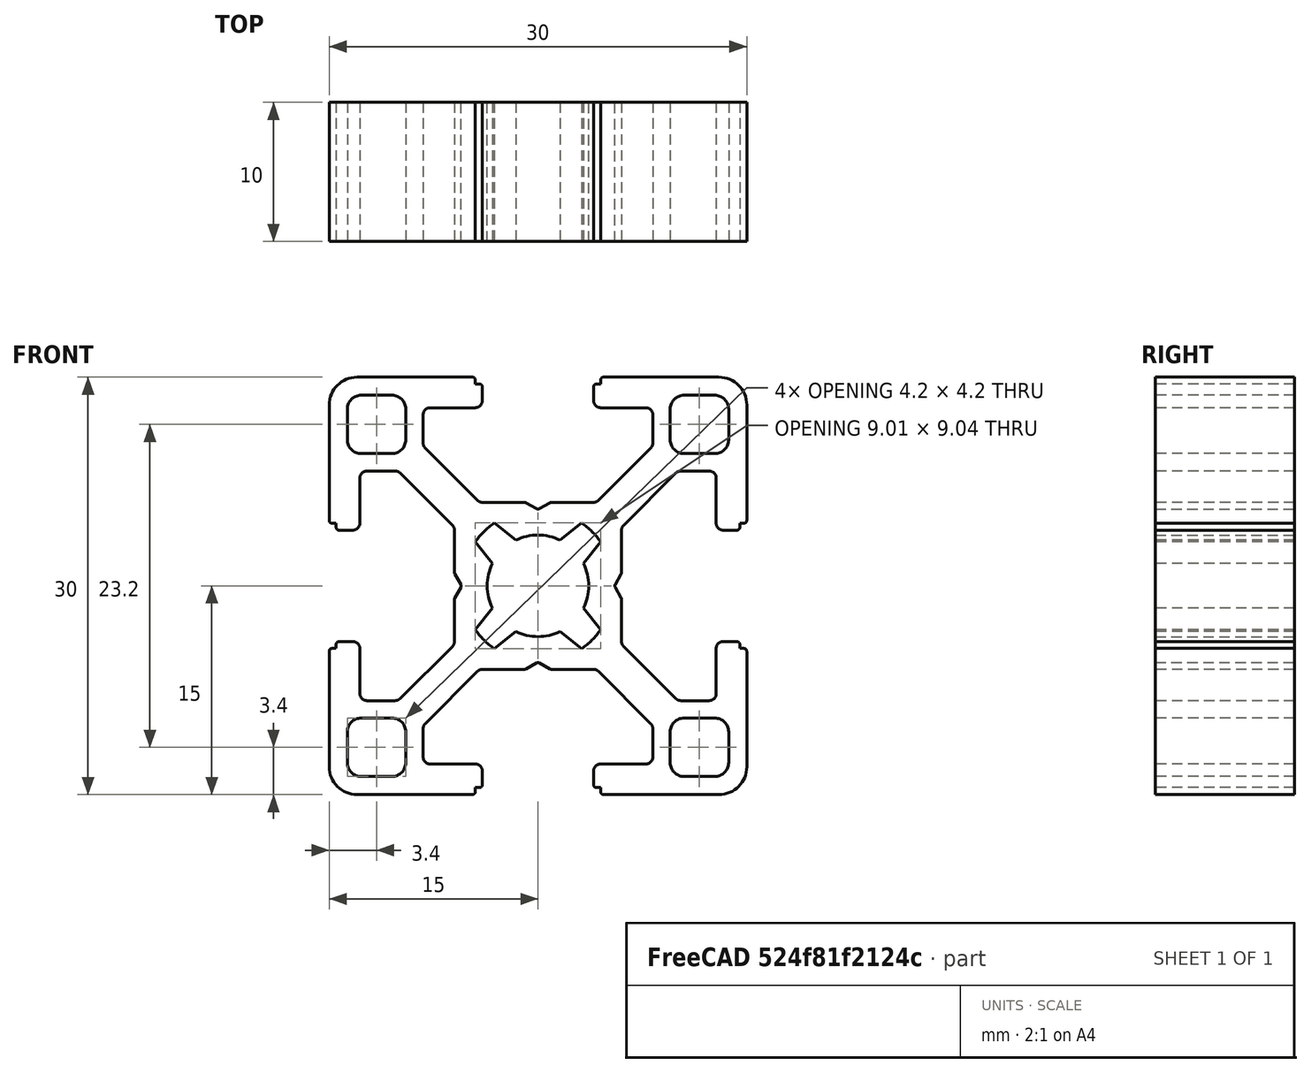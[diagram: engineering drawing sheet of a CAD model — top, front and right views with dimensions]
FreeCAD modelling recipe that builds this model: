
FCSTD DOCUMENT  (FreeCAD 0.19R21329 (Git))
Label: AP3030S8
Comment: FreeCAD-Library by episource -- https://github.com/episource/FreeCAD-Library
License: Creative Commons Attribution
LicenseURL: http://creativecommons.org/licenses/by/4.0/
objects: PartDesign::CoordinateSystem×15, TechDraw::DrawViewDimension×6, Sketcher::SketchObject×1, TechDraw::DrawSVGTemplate×1, PartDesign::Pad×1, PartDesign::Body×1, TechDraw::DrawViewPart×1, TechDraw::DrawViewClip×1, TechDraw::DrawPage×1, PartDesign::Line×1, App::DocumentObjectGroup×1, App::Part×1
note: 20 computed .brp shape members not serialized (recipe doc carries the construction recipe); baked Part::Feature solids carry a one-line shape summary decoded from their .brp

FEATURE [Sketcher::SketchObject] Sketch007  label="AP3030N8"
  MapMode = 3
  Placement = pos=(0,0,0) rot=(1,0,0;1.5708rad)
  sketch-geometry (184):
    g0: LineSegment StartX=15 StartY=13 StartZ=0 EndX=15 EndY=4.7 EndZ=0
    g1: ArcOfCircle CenterX=13 CenterY=13 CenterZ=0 NormalX=0 NormalY=0 NormalZ=1 AngleXU=2.16005e-11 Radius=2 StartAngle=0 EndAngle=1.5708
    g2: LineSegment StartX=4.7 StartY=15 StartZ=0 EndX=13 EndY=15 EndZ=0
    g3: ArcOfCircle CenterX=4.7 CenterY=14.8 CenterZ=0 NormalX=0 NormalY=0 NormalZ=1 AngleXU=1.5708 Radius=0.2 StartAngle=0 EndAngle=1.5708
    g4: LineSegment StartX=4.5 StartY=14.5 StartZ=0 EndX=4.5 EndY=14.8 EndZ=0
    g5: LineSegment StartX=4.2 StartY=14.5 StartZ=0 EndX=4.5 EndY=14.5 EndZ=0
    g6: ArcOfCircle CenterX=4.2 CenterY=14.3 CenterZ=0 NormalX=0 NormalY=0 NormalZ=1 AngleXU=1.5708 Radius=0.2 StartAngle=0 EndAngle=1.5708
    g7: LineSegment StartX=4 StartY=13.3 StartZ=0 EndX=4 EndY=14.3 EndZ=0
    g8: ArcOfCircle CenterX=4.5 CenterY=13.3 CenterZ=0 NormalX=0 NormalY=0 NormalZ=1 AngleXU=3.14159 Radius=0.5 StartAngle=0 EndAngle=1.5708
    g9: LineSegment StartX=7.75 StartY=12.8 StartZ=0 EndX=4.5 EndY=12.8 EndZ=0
    g10: ArcOfCircle CenterX=7.75 CenterY=12.3 CenterZ=0 NormalX=0 NormalY=0 NormalZ=1 AngleXU=-3.14159 Radius=0.5 StartAngle=3.14159 EndAngle=4.71239
    g11: LineSegment StartX=8.25 StartY=10.2569 StartZ=0 EndX=8.25 EndY=12.3 EndZ=0
    g12: ArcOfCircle CenterX=7.75 CenterY=10.2569 CenterZ=0 NormalX=0 NormalY=0 NormalZ=1 AngleXU=2.35675 Radius=0.5 StartAngle=3.14159 EndAngle=3.92644
    g13: LineSegment StartX=4.35095 StartY=6.14664 StartZ=0 EndX=8.10375 EndY=9.90359 EndZ=0
    g14: ArcOfCircle CenterX=3.9972 CenterY=6.5 CenterZ=0 NormalX=0 NormalY=0 NormalZ=1 AngleXU=1.5708 Radius=0.5 StartAngle=3.14159 EndAngle=3.92754
    g15: LineSegment StartX=0.953191 StartY=6 StartZ=0 EndX=3.9972 EndY=6 EndZ=0
    g16: ArcOfCircle CenterX=0.953191 CenterY=5.8 CenterZ=0 NormalX=0 NormalY=0 NormalZ=1 AngleXU=1.5708 Radius=0.2 StartAngle=0 EndAngle=0.519868
    g17: LineSegment StartX=0.0993536 StartY=5.54172 StartZ=0 EndX=0.853837 EndY=5.97358 EndZ=0
    g18: ArcOfCircle CenterX=4.3595e-07 CenterY=5.7153 CenterZ=0 NormalX=0 NormalY=0 NormalZ=1 AngleXU=1.05093 Radius=0.2 StartAngle=3.14159 EndAngle=4.18133
    g19: LineSegment StartX=-0.853837 StartY=5.97358 StartZ=0 EndX=-0.0993527 EndY=5.54172 EndZ=0
    g20: ArcOfCircle CenterX=-0.95319 CenterY=5.8 CenterZ=0 NormalX=0 NormalY=0 NormalZ=1 AngleXU=1.05093 Radius=0.2 StartAngle=0 EndAngle=0.519868
    g21: LineSegment StartX=-3.9972 StartY=6 StartZ=0 EndX=-0.95319 EndY=6 EndZ=0
    g22: ArcOfCircle CenterX=-3.9972 CenterY=6.5 CenterZ=0 NormalX=0 NormalY=0 NormalZ=1 AngleXU=0.784847 Radius=0.5 StartAngle=3.14159 EndAngle=3.92754
    g23: LineSegment StartX=-8.10375 StartY=9.90359 StartZ=0 EndX=-4.35095 EndY=6.14664 EndZ=0
    g24: ArcOfCircle CenterX=-7.75 CenterY=10.2569 CenterZ=0 NormalX=0 NormalY=0 NormalZ=1 AngleXU=1.25056e-11 Radius=0.5 StartAngle=3.14159 EndAngle=3.92644
    g25: LineSegment StartX=-8.25 StartY=12.3 StartZ=0 EndX=-8.25 EndY=10.2569 EndZ=0
    g26: ArcOfCircle CenterX=-7.75 CenterY=12.3 CenterZ=0 NormalX=0 NormalY=0 NormalZ=1 AngleXU=-1.5708 Radius=0.5 StartAngle=3.14159 EndAngle=4.71239
    g27: LineSegment StartX=-4.5 StartY=12.8 StartZ=0 EndX=-7.75 EndY=12.8 EndZ=0
    g28: ArcOfCircle CenterX=-4.5 CenterY=13.3 CenterZ=0 NormalX=0 NormalY=0 NormalZ=1 AngleXU=-1.5708 Radius=0.5 StartAngle=0 EndAngle=1.5708
    g29: LineSegment StartX=-4 StartY=14.3 StartZ=0 EndX=-4 EndY=13.3 EndZ=0
    g30: ArcOfCircle CenterX=-4.2 CenterY=14.3 CenterZ=0 NormalX=0 NormalY=0 NormalZ=1 AngleXU=0 Radius=0.2 StartAngle=0 EndAngle=1.5708
    g31: LineSegment StartX=-4.5 StartY=14.5 StartZ=0 EndX=-4.2 EndY=14.5 EndZ=0
    g32: LineSegment StartX=-4.5 StartY=14.8 StartZ=0 EndX=-4.5 EndY=14.5 EndZ=0
    g33: ArcOfCircle CenterX=-4.7 CenterY=14.8 CenterZ=0 NormalX=0 NormalY=0 NormalZ=1 AngleXU=-3.9222e-10 Radius=0.2 StartAngle=0 EndAngle=1.5708
    g34: LineSegment StartX=-13 StartY=15 StartZ=0 EndX=-4.7 EndY=15 EndZ=0
    g35: ArcOfCircle CenterX=-13 CenterY=13 CenterZ=0 NormalX=0 NormalY=0 NormalZ=1 AngleXU=1.5708 Radius=2 StartAngle=0 EndAngle=1.5708
    g36: LineSegment StartX=-15 StartY=4.7 StartZ=0 EndX=-15 EndY=13 EndZ=0
    g37: ArcOfCircle CenterX=-14.8 CenterY=4.7 CenterZ=0 NormalX=0 NormalY=0 NormalZ=1 AngleXU=-3.14159 Radius=0.2 StartAngle=0 EndAngle=1.5708
    g38: LineSegment StartX=-14.5 StartY=4.5 StartZ=0 EndX=-14.8 EndY=4.5 EndZ=0
    g39: LineSegment StartX=-14.5 StartY=4.2 StartZ=0 EndX=-14.5 EndY=4.5 EndZ=0
    g40: ArcOfCircle CenterX=-14.3 CenterY=4.2 CenterZ=0 NormalX=0 NormalY=0 NormalZ=1 AngleXU=-3.14159 Radius=0.2 StartAngle=0 EndAngle=1.5708
    g41: LineSegment StartX=-13.3 StartY=4 StartZ=0 EndX=-14.3 EndY=4 EndZ=0
    g42: ArcOfCircle CenterX=-13.3 CenterY=4.5 CenterZ=0 NormalX=0 NormalY=0 NormalZ=1 AngleXU=-1.5708 Radius=0.5 StartAngle=0 EndAngle=1.5708
    g43: LineSegment StartX=-12.8 StartY=7.75 StartZ=0 EndX=-12.8 EndY=4.5 EndZ=0
    g44: ArcOfCircle CenterX=-12.3 CenterY=7.75 CenterZ=0 NormalX=0 NormalY=0 NormalZ=1 AngleXU=-1.5708 Radius=0.5 StartAngle=3.14159 EndAngle=4.71239
    g45: LineSegment StartX=-10.2569 StartY=8.25 StartZ=0 EndX=-12.3 EndY=8.25 EndZ=0
    g46: ArcOfCircle CenterX=-10.2569 CenterY=7.75 CenterZ=0 NormalX=0 NormalY=0 NormalZ=1 AngleXU=-2.35564 Radius=0.5 StartAngle=3.14159 EndAngle=3.92644
    g47: LineSegment StartX=-6.14664 StartY=4.35095 StartZ=0 EndX=-9.90359 EndY=8.10375 EndZ=0
    g48: ArcOfCircle CenterX=-6.5 CenterY=3.9972 CenterZ=0 NormalX=0 NormalY=0 NormalZ=1 AngleXU=-3.14159 Radius=0.5 StartAngle=3.14159 EndAngle=3.92754
    g49: LineSegment StartX=-6 StartY=0.95319 StartZ=0 EndX=-6 EndY=3.9972 EndZ=0
    g50: ArcOfCircle CenterX=-5.8 CenterY=0.95319 CenterZ=0 NormalX=0 NormalY=0 NormalZ=1 AngleXU=-3.14159 Radius=0.2 StartAngle=0 EndAngle=0.519868
    g51: LineSegment StartX=-5.54172 StartY=0.0993532 StartZ=0 EndX=-5.97358 EndY=0.853837 EndZ=0
    g52: ArcOfCircle CenterX=-5.7153 CenterY=-1.603e-10 CenterZ=0 NormalX=0 NormalY=0 NormalZ=1 AngleXU=2.62172 Radius=0.2 StartAngle=3.14159 EndAngle=4.18133
    g53: LineSegment StartX=-5.97358 StartY=-0.853837 StartZ=0 EndX=-5.54172 EndY=-0.0993532 EndZ=0
    g54: ArcOfCircle CenterX=-5.8 CenterY=-0.95319 CenterZ=0 NormalX=0 NormalY=0 NormalZ=1 AngleXU=2.62172 Radius=0.2 StartAngle=0 EndAngle=0.519868
    g55: LineSegment StartX=-6 StartY=-3.9972 StartZ=0 EndX=-6 EndY=-0.95319 EndZ=0
    g56: ArcOfCircle CenterX=-6.5 CenterY=-3.9972 CenterZ=0 NormalX=0 NormalY=0 NormalZ=1 AngleXU=2.35564 Radius=0.5 StartAngle=3.14159 EndAngle=3.92754
    g57: LineSegment StartX=-9.90359 StartY=-8.10375 StartZ=0 EndX=-6.14664 EndY=-4.35095 EndZ=0
    g58: ArcOfCircle CenterX=-10.2569 CenterY=-7.75 CenterZ=0 NormalX=0 NormalY=0 NormalZ=1 AngleXU=1.5708 Radius=0.5 StartAngle=3.14159 EndAngle=3.92644
    g59: LineSegment StartX=-12.3 StartY=-8.25 StartZ=0 EndX=-10.2569 EndY=-8.25 EndZ=0
    g60: ArcOfCircle CenterX=-12.3 CenterY=-7.75 CenterZ=0 NormalX=0 NormalY=0 NormalZ=1 AngleXU=1.13687e-11 Radius=0.5 StartAngle=3.14159 EndAngle=4.71239
    g61: LineSegment StartX=-12.8 StartY=-4.5 StartZ=0 EndX=-12.8 EndY=-7.75 EndZ=0
    g62: ArcOfCircle CenterX=-13.3 CenterY=-4.5 CenterZ=0 NormalX=0 NormalY=0 NormalZ=1 AngleXU=2.2737e-12 Radius=0.5 StartAngle=0 EndAngle=1.5708
    g63: LineSegment StartX=-14.3 StartY=-4 StartZ=0 EndX=-13.3 EndY=-4 EndZ=0
    g64: ArcOfCircle CenterX=-14.3 CenterY=-4.2 CenterZ=0 NormalX=0 NormalY=0 NormalZ=1 AngleXU=1.5708 Radius=0.2 StartAngle=0 EndAngle=1.5708
    g65: LineSegment StartX=-14.5 StartY=-4.5 StartZ=0 EndX=-14.5 EndY=-4.2 EndZ=0
    g66: LineSegment StartX=-14.8 StartY=-4.5 StartZ=0 EndX=-14.5 EndY=-4.5 EndZ=0
    g67: ArcOfCircle CenterX=-14.8 CenterY=-4.7 CenterZ=0 NormalX=0 NormalY=0 NormalZ=1 AngleXU=1.5708 Radius=0.2 StartAngle=0 EndAngle=1.5708
    g68: LineSegment StartX=-15 StartY=-13 StartZ=0 EndX=-15 EndY=-4.7 EndZ=0
    g69: ArcOfCircle CenterX=-13 CenterY=-13 CenterZ=0 NormalX=0 NormalY=0 NormalZ=1 AngleXU=-3.14159 Radius=2 StartAngle=0 EndAngle=1.5708
    g70: LineSegment StartX=-4.7 StartY=-15 StartZ=0 EndX=-13 EndY=-15 EndZ=0
    g71: ArcOfCircle CenterX=-4.7 CenterY=-14.8 CenterZ=0 NormalX=0 NormalY=0 NormalZ=1 AngleXU=-1.5708 Radius=0.2 StartAngle=0 EndAngle=1.5708
    g72: LineSegment StartX=-4.5 StartY=-14.5 StartZ=0 EndX=-4.5 EndY=-14.8 EndZ=0
    g73: LineSegment StartX=-4.2 StartY=-14.5 StartZ=0 EndX=-4.5 EndY=-14.5 EndZ=0
    g74: ArcOfCircle CenterX=-4.2 CenterY=-14.3 CenterZ=0 NormalX=0 NormalY=0 NormalZ=1 AngleXU=-1.5708 Radius=0.2 StartAngle=0 EndAngle=1.5708
    g75: LineSegment StartX=-4 StartY=-13.3 StartZ=0 EndX=-4 EndY=-14.3 EndZ=0
    g76: ArcOfCircle CenterX=-4.5 CenterY=-13.3 CenterZ=0 NormalX=0 NormalY=0 NormalZ=1 AngleXU=-1.13687e-11 Radius=0.5 StartAngle=0 EndAngle=1.5708
    g77: LineSegment StartX=-7.75 StartY=-12.8 StartZ=0 EndX=-4.5 EndY=-12.8 EndZ=0
    g78: ArcOfCircle CenterX=-7.75 CenterY=-12.3 CenterZ=0 NormalX=0 NormalY=0 NormalZ=1 AngleXU=1.13687e-11 Radius=0.5 StartAngle=3.14159 EndAngle=4.71239
    g79: LineSegment StartX=-8.25 StartY=-10.2569 StartZ=0 EndX=-8.25 EndY=-12.3 EndZ=0
    g80: ArcOfCircle CenterX=-7.75 CenterY=-10.2569 CenterZ=0 NormalX=0 NormalY=0 NormalZ=1 AngleXU=-0.784847 Radius=0.5 StartAngle=3.14159 EndAngle=3.92644
    g81: LineSegment StartX=-4.35095 StartY=-6.14664 StartZ=0 EndX=-8.10375 EndY=-9.90359 EndZ=0
    g82: ArcOfCircle CenterX=-3.9972 CenterY=-6.5 CenterZ=0 NormalX=0 NormalY=0 NormalZ=1 AngleXU=-1.5708 Radius=0.5 StartAngle=3.14159 EndAngle=3.92754
    g83: LineSegment StartX=-0.95319 StartY=-6 StartZ=0 EndX=-3.9972 EndY=-6 EndZ=0
    g84: ArcOfCircle CenterX=-0.95319 CenterY=-5.8 CenterZ=0 NormalX=0 NormalY=0 NormalZ=1 AngleXU=-1.5708 Radius=0.2 StartAngle=0 EndAngle=0.519868
    g85: LineSegment StartX=-0.0993527 StartY=-5.54172 StartZ=0 EndX=-0.853837 EndY=-5.97358 EndZ=0
    g86: ArcOfCircle CenterX=4.36074e-07 CenterY=-5.7153 CenterZ=0 NormalX=0 NormalY=0 NormalZ=1 AngleXU=-2.09066 Radius=0.2 StartAngle=3.14159 EndAngle=4.18133
    g87: LineSegment StartX=0.853837 StartY=-5.97358 StartZ=0 EndX=0.0993536 EndY=-5.54172 EndZ=0
    g88: ArcOfCircle CenterX=0.953191 CenterY=-5.8 CenterZ=0 NormalX=0 NormalY=0 NormalZ=1 AngleXU=-2.09066 Radius=0.2 StartAngle=0 EndAngle=0.519868
    g89: LineSegment StartX=3.9972 StartY=-6 StartZ=0 EndX=0.953191 EndY=-6 EndZ=0
    g90: ArcOfCircle CenterX=3.9972 CenterY=-6.5 CenterZ=0 NormalX=0 NormalY=0 NormalZ=1 AngleXU=-2.35675 Radius=0.5 StartAngle=3.14159 EndAngle=3.92754
    g91: LineSegment StartX=8.10375 StartY=-9.90359 StartZ=0 EndX=4.35095 EndY=-6.14664 EndZ=0
    g92: ArcOfCircle CenterX=7.75 CenterY=-10.2569 CenterZ=0 NormalX=0 NormalY=0 NormalZ=1 AngleXU=-3.14159 Radius=0.5 StartAngle=3.14159 EndAngle=3.92644
    g93: LineSegment StartX=8.25 StartY=-12.3 StartZ=0 EndX=8.25 EndY=-10.2569 EndZ=0
    g94: ArcOfCircle CenterX=7.75 CenterY=-12.3 CenterZ=0 NormalX=0 NormalY=0 NormalZ=1 AngleXU=1.5708 Radius=0.5 StartAngle=3.14159 EndAngle=4.71239
    g95: LineSegment StartX=4.5 StartY=-12.8 StartZ=0 EndX=7.75 EndY=-12.8 EndZ=0
    g96: ArcOfCircle CenterX=4.5 CenterY=-13.3 CenterZ=0 NormalX=0 NormalY=0 NormalZ=1 AngleXU=1.5708 Radius=0.5 StartAngle=0 EndAngle=1.5708
    g97: LineSegment StartX=4 StartY=-14.3 StartZ=0 EndX=4 EndY=-13.3 EndZ=0
    g98: ArcOfCircle CenterX=4.2 CenterY=-14.3 CenterZ=0 NormalX=0 NormalY=0 NormalZ=1 AngleXU=-3.14159 Radius=0.2 StartAngle=0 EndAngle=1.5708
    g99: LineSegment StartX=4.5 StartY=-14.5 StartZ=0 EndX=4.2 EndY=-14.5 EndZ=0
    g100: LineSegment StartX=4.5 StartY=-14.8 StartZ=0 EndX=4.5 EndY=-14.5 EndZ=0
    g101: ArcOfCircle CenterX=4.7 CenterY=-14.8 CenterZ=0 NormalX=0 NormalY=0 NormalZ=1 AngleXU=3.14159 Radius=0.2 StartAngle=0 EndAngle=1.5708
    g102: LineSegment StartX=13 StartY=-15 StartZ=0 EndX=4.7 EndY=-15 EndZ=0
    g103: ArcOfCircle CenterX=13 CenterY=-13 CenterZ=0 NormalX=0 NormalY=0 NormalZ=1 AngleXU=-1.5708 Radius=2 StartAngle=-5.151e-13 EndAngle=1.5708
    g104: LineSegment StartX=15 StartY=-4.7 StartZ=0 EndX=15 EndY=-13 EndZ=0
    g105: ArcOfCircle CenterX=14.8 CenterY=-4.7 CenterZ=0 NormalX=0 NormalY=0 NormalZ=1 AngleXU=0 Radius=0.2 StartAngle=0 EndAngle=1.5708
    g106: LineSegment StartX=14.5 StartY=-4.5 StartZ=0 EndX=14.8 EndY=-4.5 EndZ=0
    g107: LineSegment StartX=14.5 StartY=-4.2 StartZ=0 EndX=14.5 EndY=-4.5 EndZ=0
    g108: ArcOfCircle CenterX=14.3 CenterY=-4.2 CenterZ=0 NormalX=0 NormalY=0 NormalZ=1 AngleXU=2.8422e-12 Radius=0.2 StartAngle=0 EndAngle=1.5708
    g109: LineSegment StartX=13.3 StartY=-4 StartZ=0 EndX=14.3 EndY=-4 EndZ=0
    g110: ArcOfCircle CenterX=13.3 CenterY=-4.5 CenterZ=0 NormalX=0 NormalY=0 NormalZ=1 AngleXU=1.5708 Radius=0.5 StartAngle=0 EndAngle=1.5708
    g111: LineSegment StartX=12.8 StartY=-7.75 StartZ=0 EndX=12.8 EndY=-4.5 EndZ=0
    g112: ArcOfCircle CenterX=12.3 CenterY=-7.75 CenterZ=0 NormalX=0 NormalY=0 NormalZ=1 AngleXU=1.5708 Radius=0.5 StartAngle=3.14159 EndAngle=4.71239
    g113: LineSegment StartX=10.2569 StartY=-8.25 StartZ=0 EndX=12.3 EndY=-8.25 EndZ=0
    g114: ArcOfCircle CenterX=10.2569 CenterY=-7.75 CenterZ=0 NormalX=0 NormalY=0 NormalZ=1 AngleXU=0.78595 Radius=0.5 StartAngle=3.14159 EndAngle=3.92644
    g115: LineSegment StartX=6.14664 StartY=-4.35095 StartZ=0 EndX=9.90359 EndY=-8.10375 EndZ=0
    g116: ArcOfCircle CenterX=6.5 CenterY=-3.9972 CenterZ=0 NormalX=0 NormalY=0 NormalZ=1 AngleXU=1.13687e-11 Radius=0.5 StartAngle=3.14159 EndAngle=3.92754
    g117: LineSegment StartX=6 StartY=-0.95319 StartZ=0 EndX=6 EndY=-3.9972 EndZ=0
    g118: ArcOfCircle CenterX=5.8 CenterY=-0.95319 CenterZ=0 NormalX=0 NormalY=0 NormalZ=1 AngleXU=1.13687e-11 Radius=0.2 StartAngle=0 EndAngle=0.519868
    g119: LineSegment StartX=5.54172 StartY=-0.0993532 StartZ=0 EndX=5.97358 EndY=-0.853837 EndZ=0
    g120: ArcOfCircle CenterX=5.7153 CenterY=-3.69482e-11 CenterZ=0 NormalX=0 NormalY=0 NormalZ=1 AngleXU=-0.519868 Radius=0.2 StartAngle=3.14159 EndAngle=4.18133
    g121: LineSegment StartX=5.97358 StartY=0.853837 StartZ=0 EndX=5.54172 EndY=0.0993532 EndZ=0
    g122: ArcOfCircle CenterX=5.8 CenterY=0.95319 CenterZ=0 NormalX=0 NormalY=0 NormalZ=1 AngleXU=-0.519868 Radius=0.2 StartAngle=0 EndAngle=0.519868
    g123: LineSegment StartX=6 StartY=3.9972 StartZ=0 EndX=6 EndY=0.95319 EndZ=0
    g124: ArcOfCircle CenterX=6.5 CenterY=3.9972 CenterZ=0 NormalX=0 NormalY=0 NormalZ=1 AngleXU=-0.78595 Radius=0.5 StartAngle=3.14159 EndAngle=3.92754
    g125: LineSegment StartX=9.90359 StartY=8.10375 StartZ=0 EndX=6.14664 EndY=4.35095 EndZ=0
    g126: ArcOfCircle CenterX=10.2569 CenterY=7.75 CenterZ=0 NormalX=0 NormalY=0 NormalZ=1 AngleXU=-1.5708 Radius=0.5 StartAngle=3.14159 EndAngle=3.92644
    g127: LineSegment StartX=12.3 StartY=8.25 StartZ=0 EndX=10.2569 EndY=8.25 EndZ=0
    g128: ArcOfCircle CenterX=12.3 CenterY=7.75 CenterZ=0 NormalX=0 NormalY=0 NormalZ=1 AngleXU=-3.14159 Radius=0.5 StartAngle=3.14159 EndAngle=4.71239
    g129: LineSegment StartX=12.8 StartY=4.5 StartZ=0 EndX=12.8 EndY=7.75 EndZ=0
    g130: ArcOfCircle CenterX=13.3 CenterY=4.5 CenterZ=0 NormalX=0 NormalY=0 NormalZ=1 AngleXU=-3.14159 Radius=0.5 StartAngle=0 EndAngle=1.5708
    g131: LineSegment StartX=14.3 StartY=4 StartZ=0 EndX=13.3 EndY=4 EndZ=0
    g132: ArcOfCircle CenterX=14.3 CenterY=4.2 CenterZ=0 NormalX=0 NormalY=0 NormalZ=1 AngleXU=-1.5708 Radius=0.2 StartAngle=0 EndAngle=1.5708
    g133: LineSegment StartX=14.5 StartY=4.5 StartZ=0 EndX=14.5 EndY=4.2 EndZ=0
    g134: LineSegment StartX=14.8 StartY=4.5 StartZ=0 EndX=14.5 EndY=4.5 EndZ=0
    g135: ArcOfCircle CenterX=14.8 CenterY=4.7 CenterZ=0 NormalX=0 NormalY=0 NormalZ=1 AngleXU=-1.5708 Radius=0.2 StartAngle=0 EndAngle=1.5708
    g136: ArcOfCircle CenterX=-10.5 CenterY=-10.5 CenterZ=0 NormalX=0 NormalY=0 NormalZ=1 AngleXU=3.14159 Radius=1 StartAngle=3.14159 EndAngle=4.71239
    g137: LineSegment StartX=-9.5 StartY=-10.5 StartZ=0 EndX=-9.5 EndY=-12.7 EndZ=0
    g138: ArcOfCircle CenterX=-10.5 CenterY=-12.7 CenterZ=0 NormalX=0 NormalY=0 NormalZ=1 AngleXU=1.5708 Radius=1 StartAngle=3.14159 EndAngle=4.71239
    g139: LineSegment StartX=-10.5 StartY=-13.7 StartZ=0 EndX=-12.7 EndY=-13.7 EndZ=0
    g140: ArcOfCircle CenterX=-12.7 CenterY=-12.7 CenterZ=0 NormalX=0 NormalY=0 NormalZ=1 AngleXU=-9.54515e-09 Radius=1 StartAngle=3.14159 EndAngle=4.71239
    g141: LineSegment StartX=-13.7 StartY=-12.7 StartZ=0 EndX=-13.7 EndY=-10.5 EndZ=0
    g142: ArcOfCircle CenterX=-12.7 CenterY=-10.5 CenterZ=0 NormalX=0 NormalY=0 NormalZ=1 AngleXU=-1.5708 Radius=1 StartAngle=3.14159 EndAngle=4.71239
    g143: LineSegment StartX=-12.7 StartY=-9.5 StartZ=0 EndX=-10.5 EndY=-9.5 EndZ=0
    g144: ArcOfCircle CenterX=10.5 CenterY=10.5 CenterZ=0 NormalX=0 NormalY=0 NormalZ=1 AngleXU=-9.58778e-09 Radius=1 StartAngle=3.14159 EndAngle=4.71239
    g145: LineSegment StartX=9.5 StartY=10.5 StartZ=0 EndX=9.5 EndY=12.7 EndZ=0
    g146: ArcOfCircle CenterX=10.5 CenterY=12.7 CenterZ=0 NormalX=0 NormalY=0 NormalZ=1 AngleXU=-1.5708 Radius=1 StartAngle=3.14159 EndAngle=4.71239
    g147: LineSegment StartX=10.5 StartY=13.7 StartZ=0 EndX=12.7 EndY=13.7 EndZ=0
    g148: ArcOfCircle CenterX=12.7 CenterY=12.7 CenterZ=0 NormalX=0 NormalY=0 NormalZ=1 AngleXU=3.14159 Radius=1 StartAngle=3.14159 EndAngle=4.71239
    g149: LineSegment StartX=13.7 StartY=12.7 StartZ=0 EndX=13.7 EndY=10.5 EndZ=0
    g150: ArcOfCircle CenterX=12.7 CenterY=10.5 CenterZ=0 NormalX=0 NormalY=0 NormalZ=1 AngleXU=1.5708 Radius=1 StartAngle=3.14159 EndAngle=4.71239
    g151: LineSegment StartX=12.7 StartY=9.5 StartZ=0 EndX=10.5 EndY=9.5 EndZ=0
    g152: ArcOfCircle CenterX=12.7 CenterY=-10.5 CenterZ=0 NormalX=0 NormalY=0 NormalZ=1 AngleXU=3.14159 Radius=1 StartAngle=3.14159 EndAngle=4.71239
    g153: LineSegment StartX=13.7 StartY=-10.5 StartZ=0 EndX=13.7 EndY=-12.7 EndZ=0
    g154: ArcOfCircle CenterX=12.7 CenterY=-12.7 CenterZ=0 NormalX=0 NormalY=0 NormalZ=1 AngleXU=1.5708 Radius=1 StartAngle=3.14159 EndAngle=4.71239
    g155: LineSegment StartX=12.7 StartY=-13.7 StartZ=0 EndX=10.5 EndY=-13.7 EndZ=0
    g156: ArcOfCircle CenterX=10.5 CenterY=-12.7 CenterZ=0 NormalX=0 NormalY=0 NormalZ=1 AngleXU=-9.61791e-09 Radius=1 StartAngle=3.14159 EndAngle=4.71239
    g157: LineSegment StartX=9.5 StartY=-12.7 StartZ=0 EndX=9.5 EndY=-10.5 EndZ=0
    g158: ArcOfCircle CenterX=10.5 CenterY=-10.5 CenterZ=0 NormalX=0 NormalY=0 NormalZ=1 AngleXU=-1.5708 Radius=1 StartAngle=3.14159 EndAngle=4.71239
    g159: LineSegment StartX=10.5 StartY=-9.5 StartZ=0 EndX=12.7 EndY=-9.5 EndZ=0
    g160: ArcOfCircle CenterX=-12.7 CenterY=10.5 CenterZ=0 NormalX=0 NormalY=0 NormalZ=1 AngleXU=-9.58607e-09 Radius=1 StartAngle=3.14159 EndAngle=4.71239
    g161: LineSegment StartX=-13.7 StartY=10.5 StartZ=0 EndX=-13.7 EndY=12.7 EndZ=0
    g162: ArcOfCircle CenterX=-12.7 CenterY=12.7 CenterZ=0 NormalX=0 NormalY=0 NormalZ=1 AngleXU=-1.5708 Radius=1 StartAngle=3.14159 EndAngle=4.71239
    g163: LineSegment StartX=-12.7 StartY=13.7 StartZ=0 EndX=-10.5 EndY=13.7 EndZ=0
    g164: ArcOfCircle CenterX=-10.5 CenterY=12.7 CenterZ=0 NormalX=0 NormalY=0 NormalZ=1 AngleXU=3.14159 Radius=1 StartAngle=3.14159 EndAngle=4.71239
    g165: LineSegment StartX=-9.5 StartY=12.7 StartZ=0 EndX=-9.5 EndY=10.5 EndZ=0
    g166: ArcOfCircle CenterX=-10.5 CenterY=10.5 CenterZ=0 NormalX=0 NormalY=0 NormalZ=1 AngleXU=1.5708 Radius=1 StartAngle=3.14159 EndAngle=4.71239
    g167: LineSegment StartX=-10.5 StartY=9.5 StartZ=0 EndX=-12.7 EndY=9.5 EndZ=0
    g168: ArcOfCircle CenterX=4.36012e-07 CenterY=-9.9476e-11 CenterZ=0 NormalX=0 NormalY=0 NormalZ=1 AngleXU=-2.0246 Radius=3.65 StartAngle=3.14159 EndAngle=4.04921
    g169: LineSegment StartX=1.60013 StartY=3.28056 StartZ=0 EndX=3.13593 EndY=4.5184 EndZ=0
    g170: ArcOfCircle CenterX=4.36012e-07 CenterY=-9.9476e-11 CenterZ=0 NormalX=0 NormalY=0 NormalZ=1 AngleXU=-2.53073 Radius=5.5 StartAngle=3.14159 EndAngle=3.49481
    g171: LineSegment StartX=4.50534 StartY=3.15467 StartZ=0 EndX=3.28056 EndY=1.60013 EndZ=0
    g172: ArcOfCircle CenterX=4.36012e-07 CenterY=-9.94742e-11 CenterZ=0 NormalX=0 NormalY=0 NormalZ=1 AngleXU=2.68778 Radius=3.65 StartAngle=3.14159 EndAngle=4.04921
    g173: LineSegment StartX=3.28056 StartY=-1.60013 StartZ=0 EndX=4.50534 EndY=-3.15467 EndZ=0
    g174: ArcOfCircle CenterX=4.36012e-07 CenterY=-9.94813e-11 CenterZ=0 NormalX=0 NormalY=0 NormalZ=1 AngleXU=2.17751 Radius=5.5 StartAngle=3.14159 EndAngle=3.49481
    g175: LineSegment StartX=3.13593 StartY=-4.5184 StartZ=0 EndX=1.60013 EndY=-3.28056 EndZ=0
    g176: ArcOfCircle CenterX=4.36012e-07 CenterY=-9.9476e-11 CenterZ=0 NormalX=0 NormalY=0 NormalZ=1 AngleXU=1.11699 Radius=3.65 StartAngle=3.14159 EndAngle=4.04921
    g177: LineSegment StartX=-1.60013 StartY=-3.28056 StartZ=0 EndX=-3.13593 EndY=-4.5184 EndZ=0
    g178: ArcOfCircle CenterX=4.36012e-07 CenterY=-9.9476e-11 CenterZ=0 NormalX=0 NormalY=0 NormalZ=1 AngleXU=0.610865 Radius=5.5 StartAngle=3.14159 EndAngle=3.49481
    g179: LineSegment StartX=-4.50534 StartY=-3.15467 StartZ=0 EndX=-3.28056 EndY=-1.60013 EndZ=0
    g180: ArcOfCircle CenterX=4.36012e-07 CenterY=-9.9476e-11 CenterZ=0 NormalX=0 NormalY=0 NormalZ=1 AngleXU=-0.453808 Radius=3.65 StartAngle=3.14159 EndAngle=4.04921
    g181: LineSegment StartX=-3.28056 StartY=1.60013 StartZ=0 EndX=-4.50534 EndY=3.15467 EndZ=0
    g182: ArcOfCircle CenterX=4.36012e-07 CenterY=-9.9476e-11 CenterZ=0 NormalX=0 NormalY=0 NormalZ=1 AngleXU=-0.964085 Radius=5.5 StartAngle=3.14159 EndAngle=3.49481
    g183: LineSegment StartX=-3.13593 StartY=4.5184 StartZ=0 EndX=-1.60013 EndY=3.28056 EndZ=0
  constraints (184):
    c: Coincident(g0,g1)
    c: Coincident(g1,g2)
    c: Coincident(g2,g3)
    c: Coincident(g3,g4)
    c: Coincident(g4,g5)
    c: Coincident(g5,g6)
    c: Coincident(g6,g7)
    c: Coincident(g7,g8)
    c: Coincident(g8,g9)
    c: Coincident(g9,g10)
    c: Coincident(g10,g11)
    c: Coincident(g11,g12)
    c: Coincident(g12,g13)
    c: Coincident(g13,g14)
    c: Coincident(g14,g15)
    c: Coincident(g15,g16)
    c: Coincident(g16,g17)
    c: Coincident(g17,g18)
    c: Coincident(g18,g19)
    c: Coincident(g19,g20)
    c: Coincident(g20,g21)
    c: Coincident(g21,g22)
    c: Coincident(g22,g23)
    c: Coincident(g23,g24)
    c: Coincident(g24,g25)
    c: Coincident(g25,g26)
    c: Coincident(g26,g27)
    c: Coincident(g27,g28)
    c: Coincident(g28,g29)
    c: Coincident(g29,g30)
    c: Coincident(g30,g31)
    c: Coincident(g31,g32)
    c: Coincident(g32,g33)
    c: Coincident(g33,g34)
    c: Coincident(g34,g35)
    c: Coincident(g35,g36)
    c: Coincident(g36,g37)
    c: Coincident(g37,g38)
    c: Coincident(g38,g39)
    c: Coincident(g39,g40)
    c: Coincident(g40,g41)
    c: Coincident(g41,g42)
    c: Coincident(g42,g43)
    c: Coincident(g43,g44)
    c: Coincident(g44,g45)
    c: Coincident(g45,g46)
    c: Coincident(g46,g47)
    c: Coincident(g47,g48)
    c: Coincident(g48,g49)
    c: Coincident(g49,g50)
    c: Coincident(g50,g51)
    c: Coincident(g51,g52)
    c: Coincident(g52,g53)
    c: Coincident(g53,g54)
    c: Coincident(g54,g55)
    c: Coincident(g55,g56)
    c: Coincident(g56,g57)
    c: Coincident(g57,g58)
    c: Coincident(g58,g59)
    c: Coincident(g59,g60)
    c: Coincident(g60,g61)
    c: Coincident(g61,g62)
    c: Coincident(g62,g63)
    c: Coincident(g63,g64)
    c: Coincident(g64,g65)
    c: Coincident(g65,g66)
    c: Coincident(g66,g67)
    c: Coincident(g67,g68)
    c: Coincident(g68,g69)
    c: Coincident(g69,g70)
    c: Coincident(g70,g71)
    c: Coincident(g71,g72)
    c: Coincident(g72,g73)
    c: Coincident(g73,g74)
    c: Coincident(g74,g75)
    c: Coincident(g75,g76)
    c: Coincident(g76,g77)
    c: Coincident(g77,g78)
    c: Coincident(g78,g79)
    c: Coincident(g79,g80)
    c: Coincident(g80,g81)
    c: Coincident(g81,g82)
    c: Coincident(g82,g83)
    c: Coincident(g83,g84)
    c: Coincident(g84,g85)
    c: Coincident(g85,g86)
    c: Coincident(g86,g87)
    c: Coincident(g87,g88)
    c: Coincident(g88,g89)
    c: Coincident(g89,g90)
    c: Coincident(g90,g91)
    c: Coincident(g91,g92)
    c: Coincident(g92,g93)
    c: Coincident(g93,g94)
    c: Coincident(g94,g95)
    c: Coincident(g95,g96)
    c: Coincident(g96,g97)
    c: Coincident(g97,g98)
    c: Coincident(g98,g99)
    c: Coincident(g99,g100)
    c: Coincident(g100,g101)
    c: Coincident(g101,g102)
    c: Coincident(g102,g103)
    c: Coincident(g103,g104)
    c: Coincident(g104,g105)
    c: Coincident(g105,g106)
    c: Coincident(g106,g107)
    c: Coincident(g107,g108)
    c: Coincident(g108,g109)
    c: Coincident(g109,g110)
    c: Coincident(g110,g111)
    c: Coincident(g111,g112)
    c: Coincident(g112,g113)
    c: Coincident(g113,g114)
    c: Coincident(g114,g115)
    c: Coincident(g115,g116)
    c: Coincident(g116,g117)
    c: Coincident(g117,g118)
    c: Coincident(g118,g119)
    c: Coincident(g119,g120)
    c: Coincident(g120,g121)
    c: Coincident(g121,g122)
    c: Coincident(g122,g123)
    c: Coincident(g123,g124)
    c: Coincident(g124,g125)
    c: Coincident(g125,g126)
    c: Coincident(g126,g127)
    c: Coincident(g127,g128)
    c: Coincident(g128,g129)
    c: Coincident(g129,g130)
    c: Coincident(g130,g131)
    c: Coincident(g131,g132)
    c: Coincident(g132,g133)
    c: Coincident(g133,g134)
    c: Coincident(g134,g135)
    c: Coincident(g135,g0)
    c: Coincident(g136,g137)
    c: Coincident(g137,g138)
    c: Coincident(g138,g139)
    c: Coincident(g139,g140)
    c: Coincident(g140,g141)
    c: Coincident(g141,g142)
    c: Coincident(g142,g143)
    c: Coincident(g143,g136)
    c: Coincident(g144,g145)
    c: Coincident(g145,g146)
    c: Coincident(g146,g147)
    c: Coincident(g147,g148)
    c: Coincident(g148,g149)
    c: Coincident(g149,g150)
    c: Coincident(g150,g151)
    c: Coincident(g151,g144)
    c: Coincident(g152,g153)
    c: Coincident(g153,g154)
    c: Coincident(g154,g155)
    c: Coincident(g155,g156)
    c: Coincident(g156,g157)
    c: Coincident(g157,g158)
    c: Coincident(g158,g159)
    c: Coincident(g159,g152)
    c: Coincident(g160,g161)
    c: Coincident(g161,g162)
    c: Coincident(g162,g163)
    c: Coincident(g163,g164)
    c: Coincident(g164,g165)
    c: Coincident(g165,g166)
    c: Coincident(g166,g167)
    c: Coincident(g167,g160)
    c: Coincident(g168,g169)
    c: Coincident(g169,g170)
    c: Coincident(g170,g171)
    c: Coincident(g171,g172)
    c: Coincident(g172,g173)
    c: Coincident(g173,g174)
    c: Coincident(g174,g175)
    c: Coincident(g175,g176)
    c: Coincident(g176,g177)
    c: Coincident(g177,g178)
    c: Coincident(g178,g179)
    c: Coincident(g179,g180)
    c: Coincident(g180,g181)
    c: Coincident(g181,g182)
    c: Coincident(g182,g183)
    c: Coincident(g183,g168)
FEATURE [TechDraw::DrawSVGTemplate] Template
  EditableTexts = FC-SC=Scale 2:1 [mm]
  Height = 210
  Orientation = 1
  Width = 297
FEATURE [PartDesign::Pad] Pad
  AllowMultiFace = false
  Length = 10
  Length2 = 100
  Midplane = true
  Placement = pos=(0,0,0) rot=(1,0,0;1.5708rad)
  Profile = -> Sketch007
  Type = 0
  expr: Length = <<Variables>>.Length
FEATURE [PartDesign::Body] Body
  Group = -> [Sketch007,Pad]
  Origin = -> Origin
  Tip = -> Pad
FEATURE [TechDraw::DrawViewPart] View
  CoarseView = false
  Direction = (0,1,0)
  Focus = 100
  HardHidden = false
  IsoCount = 0
  IsoHidden = false
  IsoVisible = false
  LockPosition = false
  Perspective = false
  Rotation = 0
  Scale = 2
  ScaleType = 0
  SeamHidden = false
  SeamVisible = false
  SmoothHidden = false
  SmoothVisible = false
  Source = -> [Body]
  X = 0
  XDirection = (-1,0,0)
  Y = 0
FEATURE [TechDraw::DrawViewClip] Clip  label="Front View"
  Height = 100
  LockPosition = false
  Rotation = 0
  Scale = 2
  ScaleType = 0
  ShowFrame = false
  Views = -> [View]
  Width = 100
  X = 148
  Y = 105
FEATURE [TechDraw::DrawViewDimension] Dimension003
  Arbitrary = false
  FormatSpec = ⌀%.1f
  Inverted = false
  LockPosition = false
  MeasureType = 1
  OverTolerance = 0
  References2D = -> [View]
  Rotation = 0
  Scale = 2
  ScaleType = 0
  TheoreticalExact = false
  Type = 5
  UnderTolerance = 0
  X = -24.5629
  Y = 3.56837
FEATURE [TechDraw::DrawViewDimension] Dimension001
  Arbitrary = false
  FormatSpec = %.1f
  Inverted = false
  LockPosition = false
  MeasureType = 1
  OverTolerance = 0
  References2D = -> [View]
  Rotation = 0
  Scale = 2
  ScaleType = 0
  TheoreticalExact = false
  Type = 2
  UnderTolerance = 0
  X = -39.3512
  Y = -20.3063
FEATURE [TechDraw::DrawViewDimension] Dimension002
  Arbitrary = false
  FormatSpec = %.1f
  Inverted = false
  LockPosition = false
  MeasureType = 1
  OverTolerance = 0
  References2D = -> [View]
  Rotation = 0
  Scale = 2
  ScaleType = 0
  TheoreticalExact = false
  Type = 2
  UnderTolerance = 0
  X = 37.004
  Y = 0.181385
FEATURE [TechDraw::DrawViewDimension] Dimension004
  Arbitrary = false
  FormatSpec = %.1f
  Inverted = false
  LockPosition = false
  MeasureType = 1
  OverTolerance = 0
  References2D = -> [View]
  Rotation = 0
  Scale = 2
  ScaleType = 0
  TheoreticalExact = false
  Type = 1
  UnderTolerance = 0
  X = 0.200781
  Y = 43.227
FEATURE [TechDraw::DrawViewDimension] Dimension005
  Arbitrary = false
  FormatSpec = %.1f
  Inverted = false
  LockPosition = false
  MeasureType = 1
  OverTolerance = 0
  References2D = -> [View]
  Rotation = 0
  Scale = 2
  ScaleType = 0
  TheoreticalExact = false
  Type = 2
  UnderTolerance = 0
  X = 2.06808
  Y = -26.6873
FEATURE [TechDraw::DrawViewDimension] Dimension
  Arbitrary = false
  FormatSpec = %.1f
  Inverted = false
  LockPosition = false
  MeasureType = 1
  OverTolerance = 0
  References2D = -> [View]
  Rotation = 0
  Scale = 2
  ScaleType = 0
  TheoreticalExact = false
  Type = 1
  UnderTolerance = 0
  X = -0.165581
  Y = 36.0381
FEATURE [TechDraw::DrawPage] Page  label="Spec"
  KeepUpdated = true
  NextBalloonIndex = 1
  ProjectionType = 0
  Scale = 2
  Template = -> Template
  Views = -> [View,Dimension001,Dimension002,Dimension003,Dimension004,Dimension,Clip,Dimension005]
FEATURE [PartDesign::Line] AssyCenter  label="AssyCenterLine"
  AttacherType = Attacher::AttachEngineLine
  Length = 20
  MapMode = 29
  Placement = pos=(0,0,0) rot=(0,0.707107,0.707107;3.14159rad)
  ResizeMode = 0
  Support = -> [Y_Axis001]
FEATURE [PartDesign::CoordinateSystem] LCS_1  label="AssyMountBackCenter"
  AttacherType = Attacher::AttachEngine3D
  AttachmentOffset = pos=(0,5,0) rot=(1,0,0;0rad)
  MapMode = 5
  Placement = pos=(0,5,0) rot=(0,0,1;0rad)
  Support = -> [XY_Plane001]
  expr: .AttachmentOffset.Base.y = <<Variables>>.Length / 2
FEATURE [PartDesign::CoordinateSystem] LCS_2  label="AssyMountFrontCenter"
  AttacherType = Attacher::AttachEngine3D
  AttachmentOffset = pos=(0,-5,0) rot=(-1,0,0;0rad)
  MapMode = 5
  Placement = pos=(0,-5,0) rot=(0,0,1;0rad)
  Support = -> [XY_Plane001]
  expr: .AttachmentOffset.Base.y = -<<Variables>>.Length / 2
FEATURE [PartDesign::CoordinateSystem] LCS_3  label="AssyMountBackTop"
  AttacherType = Attacher::AttachEngine3D
  AttachmentOffset = pos=(0,5,15) rot=(1,0,0;0rad)
  MapMode = 5
  Placement = pos=(0,5,15) rot=(0,0,1;0rad)
  Support = -> [XY_Plane001]
  expr: .AttachmentOffset.Base.z = <<Variables>>.Width / 2
  expr: .AttachmentOffset.Base.y = <<Variables>>.Length / 2
FEATURE [PartDesign::CoordinateSystem] LCS_4  label="AssyMountBackRight"
  AttacherType = Attacher::AttachEngine3D
  AttachmentOffset = pos=(15,5,0) rot=(0,1,0;1.5708rad)
  MapMode = 5
  Placement = pos=(15,5,0) rot=(0,1,0;1.5708rad)
  Support = -> [XY_Plane001]
  expr: .AttachmentOffset.Base.y = <<Variables>>.Length / 2
  expr: .AttachmentOffset.Base.x = <<Variables>>.Width / 2
FEATURE [PartDesign::CoordinateSystem] LCS_5  label="AssyMountBackBottom"
  AttacherType = Attacher::AttachEngine3D
  AttachmentOffset = pos=(0,5,-15) rot=(0,1,0;3.14159rad)
  MapMode = 5
  Placement = pos=(0,5,-15) rot=(0,1,0;3.14159rad)
  Support = -> [XY_Plane001]
  expr: .AttachmentOffset.Base.z = -<<Variables>>.Width / 2
  expr: .AttachmentOffset.Base.y = <<Variables>>.Length / 2
FEATURE [PartDesign::CoordinateSystem] LCS_6  label="AssyMountBackLeft"
  AttacherType = Attacher::AttachEngine3D
  AttachmentOffset = pos=(-15,5,0) rot=(0,1,0;4.71239rad)
  MapMode = 5
  Placement = pos=(-15,5,0) rot=(0,1,0;4.71239rad)
  Support = -> [XY_Plane001]
  expr: .AttachmentOffset.Base.x = -<<Variables>>.Width / 2
  expr: .AttachmentOffset.Base.y = <<Variables>>.Length / 2
FEATURE [PartDesign::CoordinateSystem] LCS_7  label="AssyMountFrontTop"
  AttacherType = Attacher::AttachEngine3D
  AttachmentOffset = pos=(0,-5,15) rot=(-1,0,0;0rad)
  MapMode = 5
  Placement = pos=(0,-5,15) rot=(0,0,1;0rad)
  Support = -> [XY_Plane001]
  expr: .AttachmentOffset.Base.z = <<Variables>>.Width / 2
  expr: .AttachmentOffset.Base.y = -<<Variables>>.Length / 2
FEATURE [PartDesign::CoordinateSystem] LCS_8  label="AssyMountFrontRight"
  AttacherType = Attacher::AttachEngine3D
  AttachmentOffset = pos=(15,-5,0) rot=(0,1,0;1.5708rad)
  MapMode = 5
  Placement = pos=(15,-5,0) rot=(0,1,0;1.5708rad)
  Support = -> [XY_Plane001]
  expr: .AttachmentOffset.Base.x = <<Variables>>.Width / 2
  expr: .AttachmentOffset.Base.y = -<<Variables>>.Length / 2
FEATURE [PartDesign::CoordinateSystem] LCS_9  label="AssyMountFrontBottom"
  AttacherType = Attacher::AttachEngine3D
  AttachmentOffset = pos=(0,-5,-15) rot=(0,1,0;3.14159rad)
  MapMode = 5
  Placement = pos=(0,-5,-15) rot=(0,1,0;3.14159rad)
  Support = -> [XY_Plane001]
  expr: .AttachmentOffset.Base.z = -<<Variables>>.Width / 2
  expr: .AttachmentOffset.Base.y = -<<Variables>>.Length / 2
FEATURE [PartDesign::CoordinateSystem] LCS_10  label="AssyMountFrontLeft"
  AttacherType = Attacher::AttachEngine3D
  AttachmentOffset = pos=(-15,-5,0) rot=(0,1,0;4.71239rad)
  MapMode = 5
  Placement = pos=(-15,-5,0) rot=(0,1,0;4.71239rad)
  Support = -> [XY_Plane001]
  expr: .AttachmentOffset.Base.x = -<<Variables>>.Width / 2
  expr: .AttachmentOffset.Base.y = -<<Variables>>.Length / 2
FEATURE [PartDesign::CoordinateSystem] LCS_11  label="AssyCenter"
  AttacherType = Attacher::AttachEngine3D
  AttachmentOffset = pos=(0,0,0) rot=(0,1,0;1.5708rad)
  MapMode = 4
  Support = -> [AssyCenter]
FEATURE [PartDesign::CoordinateSystem] LCS_012  label="AssyCenterTop"
  AttacherType = Attacher::AttachEngine3D
  AttachmentOffset = pos=(0,0,15) rot=(0,0,1;0rad)
  MapMode = 2
  Placement = pos=(3.3e-15,3.3e-15,15) rot=(0,0,1;0rad)
  Support = -> [LCS_11]
  expr: .AttachmentOffset.Base.z = <<Variables>>.Width / 2
FEATURE [PartDesign::CoordinateSystem] LCS_013  label="AssyCenterRight"
  AttacherType = Attacher::AttachEngine3D
  AttachmentOffset = pos=(15,0,0) rot=(0,1,0;1.5708rad)
  MapMode = 2
  Placement = pos=(15,-1.7e-15,-3.3e-15) rot=(0,1,0;1.5708rad)
  Support = -> [LCS_11]
  expr: .AttachmentOffset.Base.x = <<Variables>>.Width / 2
FEATURE [PartDesign::CoordinateSystem] LCS_015  label="AssyCenterLeft"
  AttacherType = Attacher::AttachEngine3D
  AttachmentOffset = pos=(-15,0,0) rot=(0,-1,0;1.5708rad)
  MapMode = 2
  Placement = pos=(-15,1.7e-15,3.3e-15) rot=(0,-1,0;1.5708rad)
  Support = -> [LCS_11]
  expr: .AttachmentOffset.Base.x = -<<Variables>>.Width / 2
FEATURE [PartDesign::CoordinateSystem] LCS_12  label="AssyCenterBottom"
  AttacherType = Attacher::AttachEngine3D
  AttachmentOffset = pos=(0,0,15) rot=(0,0,1;0rad)
  MapMode = 2
  Placement = pos=(-3.3e-15,-3.3e-15,-15) rot=(0,1,0;3.14159rad)
  Support = -> [LCS_11]
  expr: .AttachmentOffset.Base.z = <<Variables>>.Width / 2
FEATURE [App::DocumentObjectGroup] Group  label="Variables"
  Length = 10
  Width = 30
FEATURE [App::Part] Part  label="AP3030S8"
  Group = -> [Body,Page,AssyCenter,LCS_1,LCS_2,LCS_3,LCS_4,LCS_5,LCS_6,LCS_7,LCS_8,LCS_9,LCS_10,LCS_11,LCS_012,LCS_013,LCS_015,LCS_12,Group]
  Origin = -> Origin001
  expr: Label2 = <<Variables>>.Length.UserString
